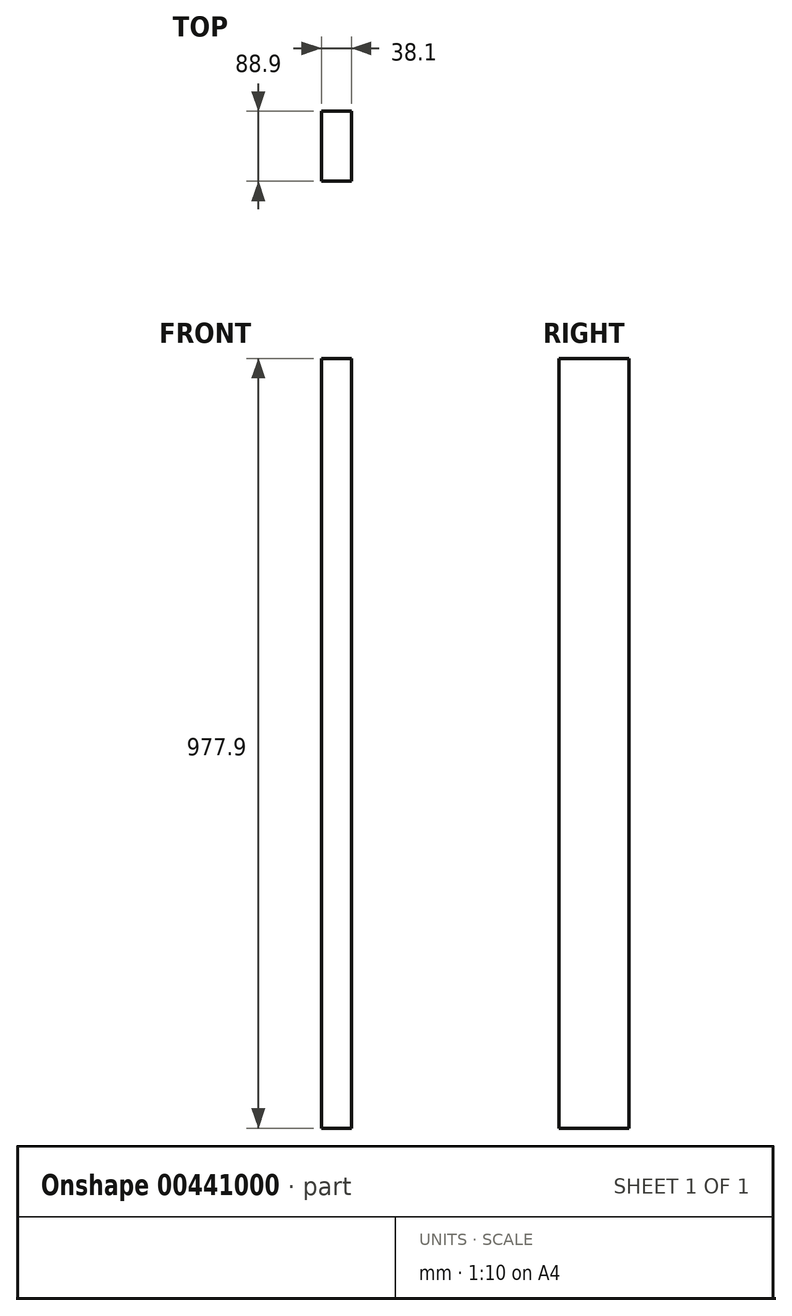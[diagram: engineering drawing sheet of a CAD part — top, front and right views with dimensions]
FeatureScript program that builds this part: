
annotation { "Feature Type Name" : "Feature", "Feature Type Description" : "" }
export const myFeature = defineFeature(function(context is Context, id is Id, definition is map)
    precondition{}
    {
        {
            var Q0;
            Q0=qCreatedBy(makeId("Right.planeOp"),FACE);
            var sketch = newSketch(context, id + "F0", { "sketchPlane" : qUnion([Q0])});
            skLineSegment(sketch, "E0.bottom", {"start": v(0, 0) * mm, "end": v(88.9, 0) * mm});
            skLineSegment(sketch, "E0.top", {"start": v(0, 977.9) * mm, "end": v(88.9, 977.9) * mm});
            skLineSegment(sketch, "E0.left", {"start": v(0, 0) * mm, "end": v(0, 977.9) * mm});
            skLineSegment(sketch, "E0.right", {"start": v(88.9, 0) * mm, "end": v(88.9, 977.9) * mm});
            skSolve(sketch);
        }
        {
            var Q0;
            Q0=makeQuery(id+"F0.imprint","IMPRINT",FACE,{"disambiguationData":[TD([[makeQuery(id+"F0.imprint","IMPRINT",EDGE,{"derivedFrom":sQuery(id+"F0.wireOp",EDGE,"E0.bottom")}),1.0]])]});
            extrude(context, id + "F1", {"entities" : qUnion([Q0]), "oppositeDirection" : true, "depth" : 38.1 * mm});
        }
    });
